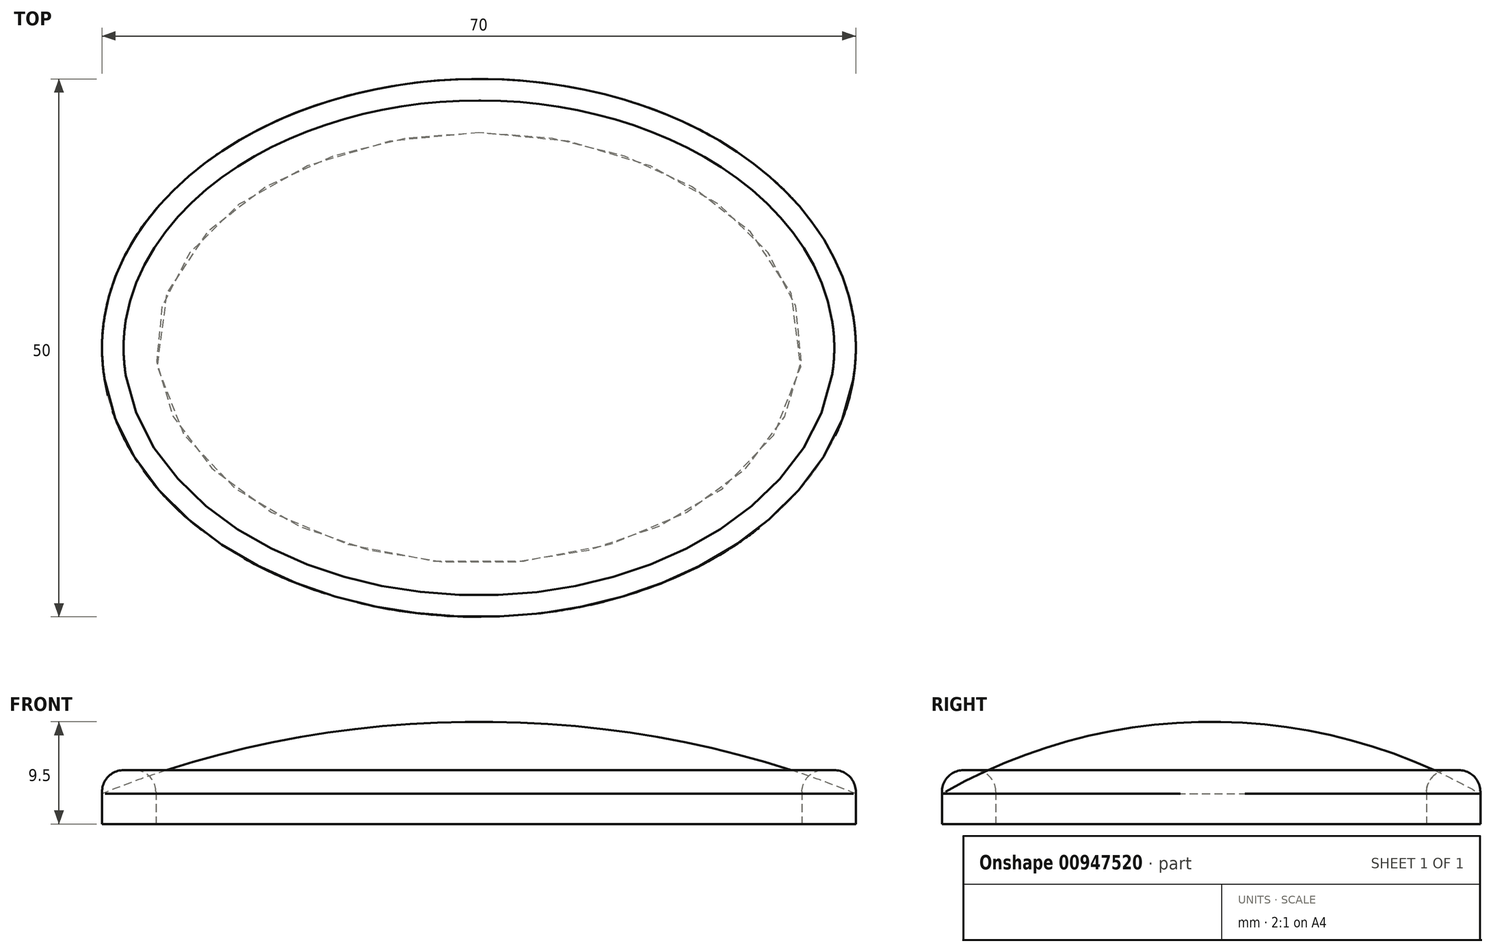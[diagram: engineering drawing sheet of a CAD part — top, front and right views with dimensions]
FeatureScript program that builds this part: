
annotation { "Feature Type Name" : "Feature", "Feature Type Description" : "" }
export const myFeature = defineFeature(function(context is Context, id is Id, definition is map)
    precondition{}
    {
        {
            var Q0;
            Q0=qCreatedBy(makeId("Top.planeOp"),FACE);
            var sketch = newSketch(context, id + "F0", { "sketchPlane" : qUnion([Q0])});
            skEllipse(sketch, "E0", {"center": v(0, 0) * mm, "majorRadius": 32.5 * mm, "minorRadius": 22.5 * mm, "majorAxis": v(1, 0)});
            skSolve(sketch);
        }
        {
            var Q0;
            Q0=qCreatedBy(makeId("Right.planeOp"),FACE);
            var sketch = newSketch(context, id + "F1", { "sketchPlane" : qUnion([Q0])});
            skLineSegment(sketch, "E1.bottom", {"start": v(25, -2.5) * mm, "end": v(20, -2.5) * mm});
            skLineSegment(sketch, "E1.top", {"start": v(25, 2.5) * mm, "end": v(20, 2.5) * mm});
            skLineSegment(sketch, "E1.left", {"start": v(25, -2.5) * mm, "end": v(25, 2.5) * mm});
            skLineSegment(sketch, "E1.right", {"start": v(20, -2.5) * mm, "end": v(20, 2.5) * mm});
            skPoint(sketch, "E1.middle", {"position": v(22.5, 0) * mm});
            skPoint(sketch, "E2.endSnap0", {"position": v(22.5, 2.5) * mm});
            skLineSegment(sketch, "E3", {"start": v(0, -2.5) * mm, "end": v(0, 2.5) * mm, "construction": true});
            skSolve(sketch);
        }
        {
            var Q0;
            Q0=qSketchRegion(id+"F1",true);
            var Q1;
            Q1=qConstructionFilter(qBodyType(qCreatedBy(id+"F0",EDGE),BodyType.WIRE),ConstructionObject.NO);
            sweep(context, id + "F2", {"profiles" : qUnion([Q0]), "path" : qUnion([Q1])});
        }
        {
            assignVariable(context, id + "F3", {"name" : "Height", "anyValue" : 100});
        }
        {
            var Q0;
            Q0=qCreatedBy(makeId("Top.planeOp"),FACE);
            cPlane(context, id + "F4", {"entities" : qUnion([Q0]), "cplaneType" : CPlaneType.OFFSET, "offset" : (getVariable(context, 'Height') / 2 - 7) * mm, "oppositeDirection" : true, "width" : 150 * mm, "height" : 150 * mm});
        }
        {
            var Q0;
            Q0=qCreatedBy(id+"F4.planeOp",FACE);
            var sketch = newSketch(context, id + "F5", { "sketchPlane" : qUnion([Q0])});
            skEllipse(sketch, "E4", {"center": v(0, 0) * mm, "majorRadius": 70 * mm, "minorRadius": 50 * mm, "majorAxis": v(1, 0)});
            skLineSegment(sketch, "E5", {"start": v(-70, 0) * mm, "end": v(70, 0) * mm});
            skSolve(sketch);
        }
        {
            var Q0;
            {var subQ0=sQuery(id+"F5.wireOp",EDGE,"E5");Q0=makeQuery(id+"F5.imprint","IMPRINT",FACE,{"disambiguationData":[TD([[makeQuery(id+"F5.imprint","IMPRINT",EDGE,{"derivedFrom":subQ0}),1.0]])]});}
            var Q1;
            Q1=sQuery(id+"F5.wireOp",EDGE,"E5");
            revolve(context, id + "F6", {"surfaceOperationType" : NewSurfaceOperationType.NEW, "entities" : qUnion([Q0]), "axis" : qUnion([Q1]), "revolveType" : RevolveType.ONE_DIRECTION, "angle" : 180 * degree});
        }
        {
            var Q0;
            Q0=qCreatedBy(id+"F4.planeOp",FACE);
            var sketch = newSketch(context, id + "F7", { "sketchPlane" : qUnion([Q0])});
            skEllipse(sketch, "E6", {"center": v(0, 0) * mm, "majorRadius": 35 * mm, "minorRadius": 25 * mm, "majorAxis": v(1, 0)});
            skSolve(sketch);
        }
        {
            var Q0;
            Q0=qSketchRegion(id+"F7",true);
            extrude(context, id + "F8", {"entities" : qUnion([Q0]), "operationType" : NewBodyOperationType.INTERSECT, "oppositeDirection" : true, "depth" : 20000 * mm, "offsetDistance" : 25 * mm, "symmetric" : true});
        }
        {
            var Q0;
            Q0=qSketchRegion(id+"F7",true);
            var Q1;
            Q1=makeQuery(id+"F2.opSweep","SWEPT_FACE",FACE,{"disambiguationData":[OSD([sQuery(id+"F0.wireOp",EDGE,"E0"),sQuery(id+"F1.wireOp",EDGE,"E1.bottom")])]});
            extrude(context, id + "F9", {"entities" : qUnion([Q0]), "operationType" : NewBodyOperationType.REMOVE, "endBound" : BoundingType.UP_TO_SURFACE, "depth" : 25 * mm, "endBoundEntityFace" : qUnion([Q1]), "offsetDistance" : 25 * mm});
        }
        {
            var Q0;
            Q0=makeQuery(id+"F2.opSweep","SWEPT_EDGE",EDGE,{"disambiguationData":[OSD([sQuery(id+"F0.wireOp",EDGE,"E0"),sQuery(id+"F1.wireOp",EDGE,"E1.top"),sQuery(id+"F1.wireOp",EDGE,"E1.left")])]});
            var Q1;
            Q1=makeQuery(id+"F2.opSweep","SWEPT_EDGE",EDGE,{"disambiguationData":[OSD([sQuery(id+"F0.wireOp",EDGE,"E0"),sQuery(id+"F1.wireOp",EDGE,"E1.top"),sQuery(id+"F1.wireOp",EDGE,"E1.right")])]});
            fillet(context, id + "F10", {"entities" : qUnion([Q0, Q1]), "radius" : 2 * mm, "tangentPropagation" : true, "allowEdgeOverflow" : false});
        }
    });
